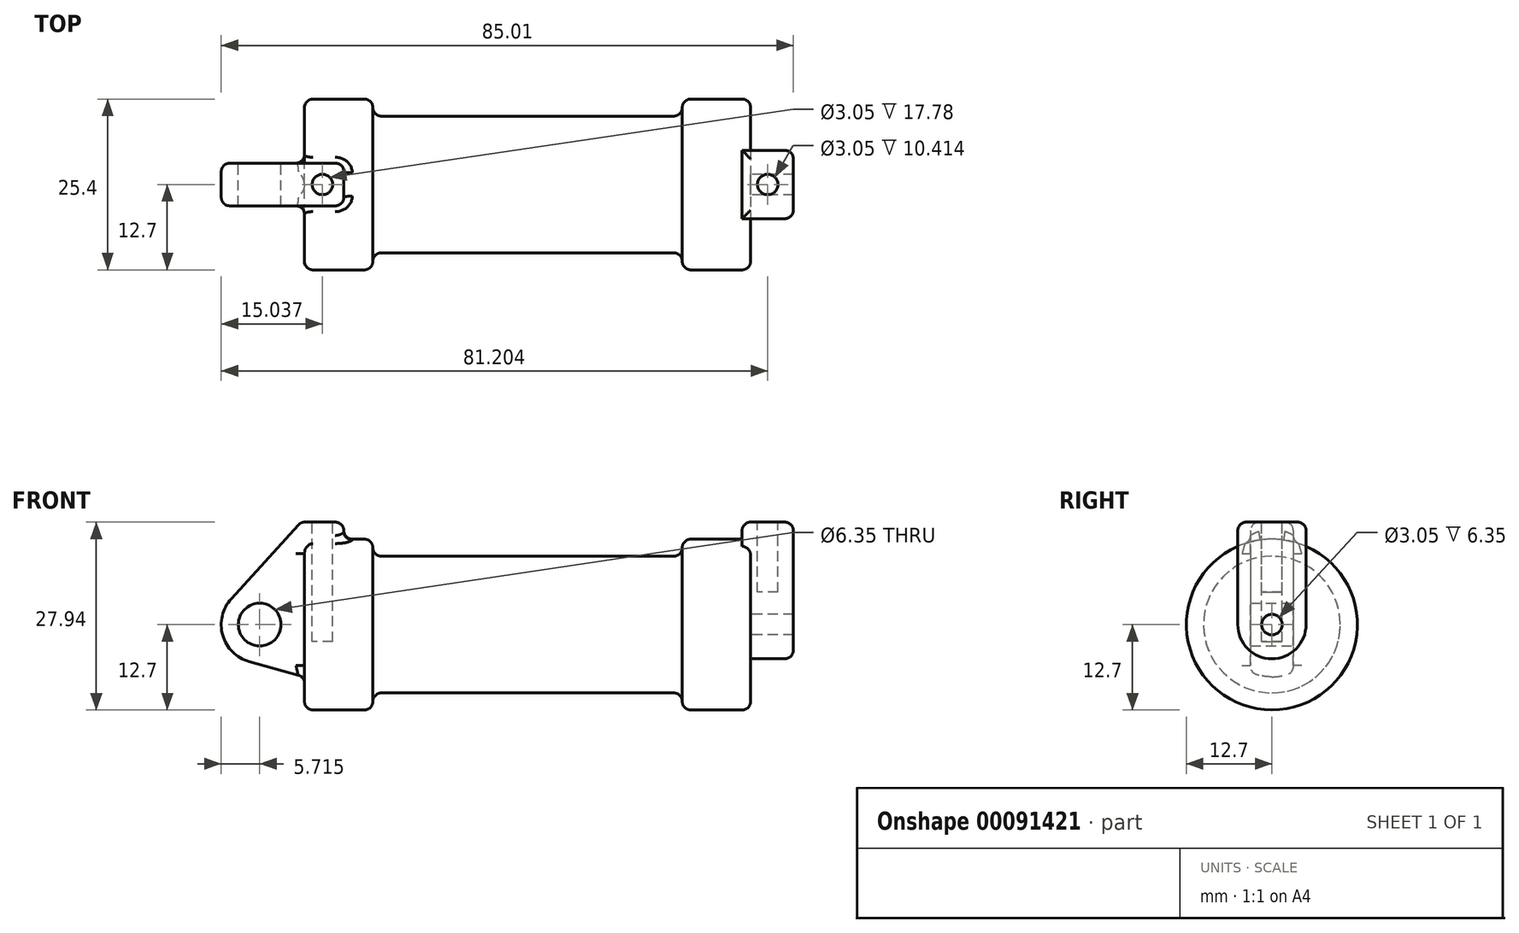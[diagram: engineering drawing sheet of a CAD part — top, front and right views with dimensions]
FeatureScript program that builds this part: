
annotation { "Feature Type Name" : "Feature", "Feature Type Description" : "" }
export const myFeature = defineFeature(function(context is Context, id is Id, definition is map)
    precondition{}
    {
        {
            var Q0;
            Q0=qCreatedBy(makeId("Front.planeOp"),FACE);
            var sketch = newSketch(context, id + "F0", { "sketchPlane" : qUnion([Q0])});
            skLineSegment(sketch, "E0", {"start": v(0, 0) * mm, "end": v(0, 11.43) * mm});
            skLineSegment(sketch, "E1", {"start": v(1.27, 12.7) * mm, "end": v(10.16, 12.7) * mm});
            skLineSegment(sketch, "E2", {"start": v(10.16, 12.7) * mm, "end": v(10.16, 10.16) * mm});
            skLineSegment(sketch, "E3", {"start": v(10.16, 10.16) * mm, "end": v(56.13, 10.16) * mm});
            skLineSegment(sketch, "E4", {"start": v(56.13, 10.16) * mm, "end": v(56.13, 12.7) * mm});
            skLineSegment(sketch, "E5", {"start": v(56.13, 12.7) * mm, "end": v(66.3, 12.7) * mm});
            skLineSegment(sketch, "E6", {"start": v(66.3, 12.7) * mm, "end": v(66.3, 0) * mm});
            skLineSegment(sketch, "E7", {"start": v(66.3, 0) * mm, "end": v(0, 0) * mm});
            skLineSegment(sketch, "E8", {"start": v(5.84, 15.24) * mm, "end": v(-0.5, 15.24) * mm});
            skLineSegment(sketch, "E9", {"start": v(-0.5, 15.24) * mm, "end": v(-10.88, 3.85) * mm});
            skLineSegment(sketch, "E10", {"start": v(0, 0) * mm, "end": v(-6.65, 0) * mm});
            skCircle(sketch, "E11", {"center": v(-6.65, 0) * mm, "radius": 5.72 * mm});
            skCircle(sketch, "E12", {"center": v(-6.65, 0) * mm, "radius": 3.18 * mm});
            skLineSegment(sketch, "E13", {"start": v(5.84, 15.24) * mm, "end": v(5.84, -9.4) * mm});
            skLineSegment(sketch, "E14", {"start": v(5.84, -9.4) * mm, "end": v(-8.18, -5.5) * mm});
            skLineSegment(sketch, "E15", {"start": v(0, 0) * mm, "end": v(0, -7.78) * mm});
            skPoint(sketch, "E16.visualSharp", {"position": v(0, 12.7) * mm});
            skArc(sketch, "E16.filletArc", {"start": v(1.27, 12.7) * mm, "mid": v(0.37, 12.33) * mm, "end": v(0, 11.43) * mm});
            skLineSegment(sketch, "E17", {"start": v(1.27, 12.7) * mm, "end": v(0, 12.7) * mm});
            skSolve(sketch);
        }
        {
            var Q0;
            {var subQ0=sQuery(id+"F0.wireOp",EDGE,"E2");Q0=makeQuery(id+"F0.imprint","IMPRINT",FACE,{"disambiguationData":[TD([[makeQuery(id+"F0.imprint","IMPRINT",EDGE,{"derivedFrom":subQ0}),-1.0]])]});}
            var Q1;
            {var subQ0=sQuery(id+"F0.wireOp",EDGE,"E0");Q1=makeQuery(id+"F0.imprint","IMPRINT",FACE,{"disambiguationData":[TD([[makeQuery(id+"F0.imprint","IMPRINT",EDGE,{"derivedFrom":subQ0}),-1.0]])]});}
            var Q2;
            Q2=sQuery(id+"F0.wireOp",EDGE,"E7");
            revolve(context, id + "F1", {"entities" : qUnion([Q0, Q1]), "axis" : qUnion([Q2]), "revolveType" : RevolveType.FULL});
        }
        {
            var Q0;
            {var subQ7=sQuery(id+"F0.wireOp",EDGE,"E0");Q0=makeQuery(id+"F0.imprint","IMPRINT",FACE,{"disambiguationData":[TD([[makeQuery(id+"F0.imprint","IMPRINT",EDGE,{"derivedFrom":subQ7}),1.0]])]});}
            var Q1;
            {var subQ5=sQuery(id+"F0.wireOp",EDGE,"E0");Q1=makeQuery(id+"F0.imprint","IMPRINT",FACE,{"disambiguationData":[TD([[makeQuery(id+"F0.imprint","IMPRINT",EDGE,{"derivedFrom":subQ5}),-1.0]])]});}
            var Q2;
            {var subQ4=sQuery(id+"F0.wireOp",EDGE,"E12");Q2=makeQuery(id+"F0.imprint","IMPRINT",FACE,{"disambiguationData":[TD([[makeQuery(id+"F0.imprint","IMPRINT",EDGE,{"derivedFrom":subQ4}),-1.0]])]});}
            var Q3;
            {var subQ0=sQuery(id+"F0.wireOp",EDGE,"E15");Q3=makeQuery(id+"F0.imprint","IMPRINT",FACE,{"disambiguationData":[TD([[makeQuery(id+"F0.imprint","IMPRINT",EDGE,{"derivedFrom":subQ0}),-1.0]])]});}
            var Q4;
            {var subQ0=sQuery(id+"F0.wireOp",EDGE,"E15");Q4=makeQuery(id+"F0.imprint","IMPRINT",FACE,{"disambiguationData":[TD([[makeQuery(id+"F0.imprint","IMPRINT",EDGE,{"derivedFrom":subQ0}),1.0]])]});}
            extrude(context, id + "F2", {"entities" : qUnion([Q0, Q1, Q2, Q3, Q4]), "operationType" : NewBodyOperationType.ADD, "endBound" : BoundingType.SYMMETRIC, "depth" : 6.35 * mm});
        }
        {
            var Q0;
            Q0=makeQuery(id+"F1.opRevolve","SWEPT_FACE",FACE,{"disambiguationData":[OSD([sQuery(id+"F0.wireOp",EDGE,"E6")])]});
            var sketch = newSketch(context, id + "F3", { "sketchPlane" : qUnion([Q0])});
            skCircle(sketch, "E18", {"center": v(0, 0) * mm, "radius": 1.52 * mm});
            skCircle(sketch, "E19", {"center": v(0, 0) * mm, "radius": 5.08 * mm});
            skLineSegment(sketch, "E20", {"start": v(-5.08, 0) * mm, "end": v(-5.08, 15.24) * mm});
            skLineSegment(sketch, "E21", {"start": v(5.08, 0) * mm, "end": v(5.08, 15.24) * mm});
            skLineSegment(sketch, "E22", {"start": v(-5.08, 15.24) * mm, "end": v(5.08, 15.24) * mm});
            skSolve(sketch);
        }
        {
            var Q0;
            Q0 = qSketchRegion(id + "F3", true);
            extrude(context, id + "F4", {"entities" : qUnion([Q0]), "operationType" : NewBodyOperationType.ADD, "depth" : 6.35 * mm});
        }
        {
            var Q0;
            Q0=makeQuery(id+"F4.opExtrude","CAP_FACE",FACE,{"disambiguationData":[OSD([sQuery(id+"F3.wireOp",EDGE,"E18"),sQuery(id+"F3.wireOp",EDGE,"E19"),sQuery(id+"F3.wireOp",EDGE,"E20"),sQuery(id+"F3.wireOp",EDGE,"E21"),sQuery(id+"F3.wireOp",EDGE,"E22")])],"isStart":true});
            extrude(context, id + "F5", {"entities" : qUnion([Q0]), "operationType" : NewBodyOperationType.ADD, "depth" : 1.27 * mm});
        }
        {
            var Q0;
            Q0=makeQuery(id+"F2.opExtrude","SWEPT_FACE",FACE,{"disambiguationData":[OSD([sQuery(id+"F0.wireOp",EDGE,"E8")])]});
            var sketch = newSketch(context, id + "F6", { "sketchPlane" : qUnion([Q0])});
            skCircle(sketch, "E23", {"center": v(2.67, 0) * mm, "radius": 1.52 * mm});
            skCircle(sketch, "E24", {"center": v(68.83, 0) * mm, "radius": 1.52 * mm});
            skSolve(sketch);
        }
        {
            var Q0;
            Q0=makeQuery(id+"F6.imprint","IMPRINT",FACE,{"disambiguationData":[TD([[makeQuery(id+"F6.imprint","IMPRINT",EDGE,{"derivedFrom":sQuery(id+"F6.wireOp",EDGE,"E23")}),1.0]])]});
            extrude(context, id + "F7", {"entities" : qUnion([Q0]), "operationType" : NewBodyOperationType.REMOVE, "oppositeDirection" : true, "depth" : 17.78 * mm});
        }
        {
            var Q0;
            Q0=makeQuery(id+"F6.imprint","IMPRINT",FACE,{"disambiguationData":[TD([[makeQuery(id+"F6.imprint","IMPRINT",EDGE,{"derivedFrom":sQuery(id+"F6.wireOp",EDGE,"E24")}),1.0]])]});
            extrude(context, id + "F8", {"entities" : qUnion([Q0]), "operationType" : NewBodyOperationType.REMOVE, "oppositeDirection" : true, "depth" : 10.4 * mm});
        }
        {
            var Q0;
            Q0=makeQuery(id+"F1.opRevolve","SWEPT_EDGE",EDGE,{"disambiguationData":[OSD([sQuery(id+"F0.wireOp",EDGE,"E3"),sQuery(id+"F0.wireOp",EDGE,"E4")])]});
            var Q1;
            Q1=makeQuery(id+"F1.opRevolve","SWEPT_EDGE",EDGE,{"disambiguationData":[OSD([sQuery(id+"F0.wireOp",EDGE,"E4"),sQuery(id+"F0.wireOp",EDGE,"E5")])]});
            var Q2;
            Q2=makeQuery(id+"F4.boolean.opBoolean","SPLIT",EDGE,{"disambiguationData":[OD(1.0)],"derivedFrom":makeQuery(id+"F1.opRevolve","SWEPT_EDGE",EDGE,{"disambiguationData":[OSD([sQuery(id+"F0.wireOp",EDGE,"E5"),sQuery(id+"F0.wireOp",EDGE,"E6")])]})});
            var Q3;
            Q3=makeQuery(id+"F4.opExtrude","CAP_EDGE",EDGE,{"disambiguationData":[OSD([sQuery(id+"F3.wireOp",EDGE,"E19")])],"isStart":false});
            var Q4;
            Q4=makeQuery(id+"F4.opExtrude","CAP_EDGE",EDGE,{"disambiguationData":[OSD([sQuery(id+"F3.wireOp",EDGE,"E22")])],"isStart":false});
            var Q5;
            {var subQ0=sQuery(id+"F3.wireOp",EDGE,"E22");var subQ1=sQuery(id+"F3.wireOp",EDGE,"E21");Q5=makeQuery(id+"F5.boolean.opBoolean","MERGE",EDGE,{"derivedFrom":[makeQuery(id+"F4.opExtrude","SWEPT_EDGE",EDGE,{"disambiguationData":[OSD([subQ1,subQ0])]}),makeQuery(id+"F5.opExtrude","SWEPT_EDGE",EDGE,{"disambiguationData":[OSD([subQ1,subQ0])]})]});}
            var Q6;
            Q6=makeQuery(id+"F5.opExtrude","CAP_EDGE",EDGE,{"disambiguationData":[OSD([sQuery(id+"F3.wireOp",EDGE,"E22")])],"isStart":false});
            var Q7;
            {var subQ0=sQuery(id+"F3.wireOp",EDGE,"E22");var subQ1=sQuery(id+"F3.wireOp",EDGE,"E20");Q7=makeQuery(id+"F5.boolean.opBoolean","MERGE",EDGE,{"derivedFrom":[makeQuery(id+"F4.opExtrude","SWEPT_EDGE",EDGE,{"disambiguationData":[OSD([subQ1,subQ0])]}),makeQuery(id+"F5.opExtrude","SWEPT_EDGE",EDGE,{"disambiguationData":[OSD([subQ1,subQ0])]})]});}
            var Q8;
            Q8=makeQuery(id+"F4.opExtrude","CAP_EDGE",EDGE,{"disambiguationData":[OSD([sQuery(id+"F3.wireOp",EDGE,"E20")])],"isStart":false});
            var Q9;
            Q9=makeQuery(id+"F4.opExtrude","CAP_EDGE",EDGE,{"disambiguationData":[OSD([sQuery(id+"F3.wireOp",EDGE,"E21")])],"isStart":false});
            var Q10;
            Q10=makeQuery(id+"F1.opRevolve","SWEPT_EDGE",EDGE,{"disambiguationData":[OSD([sQuery(id+"F0.wireOp",EDGE,"E2"),sQuery(id+"F0.wireOp",EDGE,"E3")])]});
            var Q11;
            Q11=makeQuery(id+"F1.opRevolve","SWEPT_EDGE",EDGE,{"disambiguationData":[OSD([sQuery(id+"F0.wireOp",EDGE,"E1"),sQuery(id+"F0.wireOp",EDGE,"E2")])]});
            var Q12;
            Q12=makeQuery(id+"F2.opExtrude","CAP_EDGE",EDGE,{"disambiguationData":[OSD([sQuery(id+"F0.wireOp",EDGE,"E8")])],"isStart":false});
            var Q13;
            Q13=makeQuery(id+"F2.opExtrude","CAP_EDGE",EDGE,{"disambiguationData":[OSD([sQuery(id+"F0.wireOp",EDGE,"E9")])],"isStart":false});
            var Q14;
            Q14=makeQuery(id+"F2.opExtrude","SWEPT_EDGE",EDGE,{"disambiguationData":[OSD([sQuery(id+"F0.wireOp",EDGE,"E8"),sQuery(id+"F0.wireOp",EDGE,"E13")])]});
            var Q15;
            Q15=makeQuery(id+"F2.opExtrude","CAP_EDGE",EDGE,{"disambiguationData":[OSD([sQuery(id+"F0.wireOp",EDGE,"E8")])],"isStart":true});
            var Q16;
            Q16=makeQuery(id+"F2.opExtrude","SWEPT_EDGE",EDGE,{"disambiguationData":[OSD([sQuery(id+"F0.wireOp",EDGE,"E8"),sQuery(id+"F0.wireOp",EDGE,"E9")])]});
            var Q17;
            {var subQ0=sQuery(id+"F0.wireOp",EDGE,"E13");Q17=makeQuery(id+"F2.opExtrude","CAP_EDGE",EDGE,{"disambiguationData":[OSD([subQ0]),TDD([makeQuery(id+"F0.imprint","IMPRINT",EDGE,{"disambiguationData":[TD([[makeQuery(id+"F0.imprint","INTERSECT",VERTEX,{"derivedFrom":[sQuery(id+"F0.wireOp",EDGE,"E8"),subQ0]}),-1.0]])],"derivedFrom":subQ0})])],"isStart":false});}
            var Q18;
            {var subQ0=sQuery(id+"F0.wireOp",EDGE,"E13");Q18=makeQuery(id+"F2.opExtrude","CAP_EDGE",EDGE,{"disambiguationData":[OSD([subQ0]),TDD([makeQuery(id+"F0.imprint","IMPRINT",EDGE,{"disambiguationData":[TD([[makeQuery(id+"F0.imprint","INTERSECT",VERTEX,{"derivedFrom":[sQuery(id+"F0.wireOp",EDGE,"E8"),subQ0]}),-1.0]])],"derivedFrom":subQ0})])],"isStart":true});}
            var Q19;
            Q19=makeQuery(id+"F2.opExtrude","CAP_EDGE",EDGE,{"disambiguationData":[OSD([sQuery(id+"F0.wireOp",EDGE,"E9")])],"isStart":true});
            var Q20;
            Q20=makeQuery(id+"F1.opRevolve","SWEPT_EDGE",EDGE,{"disambiguationData":[OSD([sQuery(id+"F0.wireOp",EDGE,"E0"),sQuery(id+"F0.wireOp",EDGE,"E1")])]});
            var Q21;
            Q21=makeQuery(id+"F4.opExtrude","CAP_EDGE",EDGE,{"disambiguationData":[OSD([sQuery(id+"F3.wireOp",EDGE,"E19")])],"isStart":true});
            var Q22;
            Q22=makeQuery(id+"F2.boolean.opBoolean","INTERSECT",EDGE,{"derivedFrom":[makeQuery(id+"F1.opRevolve","SWEPT_FACE",FACE,{"disambiguationData":[OSD([sQuery(id+"F0.wireOp",EDGE,"E1")])]}),makeQuery(id+"F2.opExtrude","CAP_FACE",FACE,{"disambiguationData":[OSD([sQuery(id+"F0.wireOp",EDGE,"E8"),sQuery(id+"F0.wireOp",EDGE,"E9"),sQuery(id+"F0.wireOp",EDGE,"E11"),sQuery(id+"F0.wireOp",EDGE,"E12"),sQuery(id+"F0.wireOp",EDGE,"E13"),sQuery(id+"F0.wireOp",EDGE,"E14")])],"isStart":false})]});
            var Q23;
            Q23=makeQuery(id+"F2.boolean.opBoolean","INTERSECT",EDGE,{"derivedFrom":[makeQuery(id+"F1.opRevolve","SWEPT_FACE",FACE,{"disambiguationData":[OSD([sQuery(id+"F0.wireOp",EDGE,"E1")])]}),makeQuery(id+"F2.opExtrude","SWEPT_FACE",FACE,{"disambiguationData":[OSD([sQuery(id+"F0.wireOp",EDGE,"E13")])]})]});
            var Q24;
            Q24=makeQuery(id+"F2.boolean.opBoolean","INTERSECT",EDGE,{"derivedFrom":[makeQuery(id+"F1.opRevolve","SWEPT_FACE",FACE,{"disambiguationData":[OSD([sQuery(id+"F0.wireOp",EDGE,"E1")])]}),makeQuery(id+"F2.opExtrude","CAP_FACE",FACE,{"disambiguationData":[OSD([sQuery(id+"F0.wireOp",EDGE,"E8"),sQuery(id+"F0.wireOp",EDGE,"E9"),sQuery(id+"F0.wireOp",EDGE,"E11"),sQuery(id+"F0.wireOp",EDGE,"E12"),sQuery(id+"F0.wireOp",EDGE,"E13"),sQuery(id+"F0.wireOp",EDGE,"E14")])],"isStart":true})]});
            fillet(context, id + "F9", {"entities" : qUnion([Q0, Q1, Q2, Q3, Q4, Q5, Q6, Q7, Q8, Q9, Q10, Q11, Q12, Q13, Q14, Q15, Q16, Q17, Q18, Q19, Q20, Q21, Q22, Q23, Q24]), "radius" : 1.27 * mm, "tangentPropagation" : true, "allowEdgeOverflow" : false});
        }
    });
